# Revit family: AM 950C HH
name_source: partatom
category: Mechanical Equipment
units: mm (PartAtom-declared; Revit-internal decimal feet)

## family parameters
Always vertical = Yes
Cut with Voids When Loaded = No
OmniClass Number = 23.75.00.00
OmniClass Title = Climate Control (HVAC)
Part Type = Normal
Room Calculation Point = No
Round Connector Dimension = Use Diameter
Shared = No
Work Plane-Based = No

## types (1)
- AM 950C HH
    BMS IN = (PTS) 2x2x0,6
    BMS Out = (PTS) 2x2x0,6
    BMS Panel = (PTS) 2x2x0,6
    Color casing = RAL 9010
    Condensate conector = Ø6/9 mm
    Electrical connection = 1  ~ 230V+N+PE / 3 ~ 230/400V+N+PE/ 50 Hz
    Exhaust Air out = 315 mm
    Manufacturer = Airmaster A/S
    Max Current = 20 A
    Max Power Consumption = 4454 W
    Max. flow rate 30 dB(A) with ePM10 50% filters = 950 m³
    Max. flow rate 30 dB(A) with ePM10 55% filters = 926 m³
    Max. flow rate 30 dB(A) with ePM10 80% filters = 903 m³
    Max. flow rate 35 dB(A) with ePM10 50% filters = 1050 m³
    Max. flow rate 35 dB(A) with ePM10 55% filters = 1025 m³
    Max. flow rate 35 dB(A) with ePM10 80% filters = 998 m³
    Maximum fuse = 16 A, 1 phase, type B or 16 A, 3 phase, type B
    Model = AM 950C HH
    Network Conection = AWG 24 CAT 5e STP
    Nominal current, air handling unit = 2,76 A
    Nominal current, electrical comfort heating surface = 7,83 A
    Nominal current, electrical preheating surface = 10 A
    Publication date = 02.06.2025
    Recommended residual current circuit breaker (RCCB) = Type B
    Suply Air In = 315 mm
    URL = www.airmaster-as.com
    Version number = 0,0
    Weight (Standard Unit) = 340
    Weight standard air handling unit, complete = 340 kg

## geometry (parser evidence)
native form markers: Sweep x6
no freeform markers — native parametric forms only
